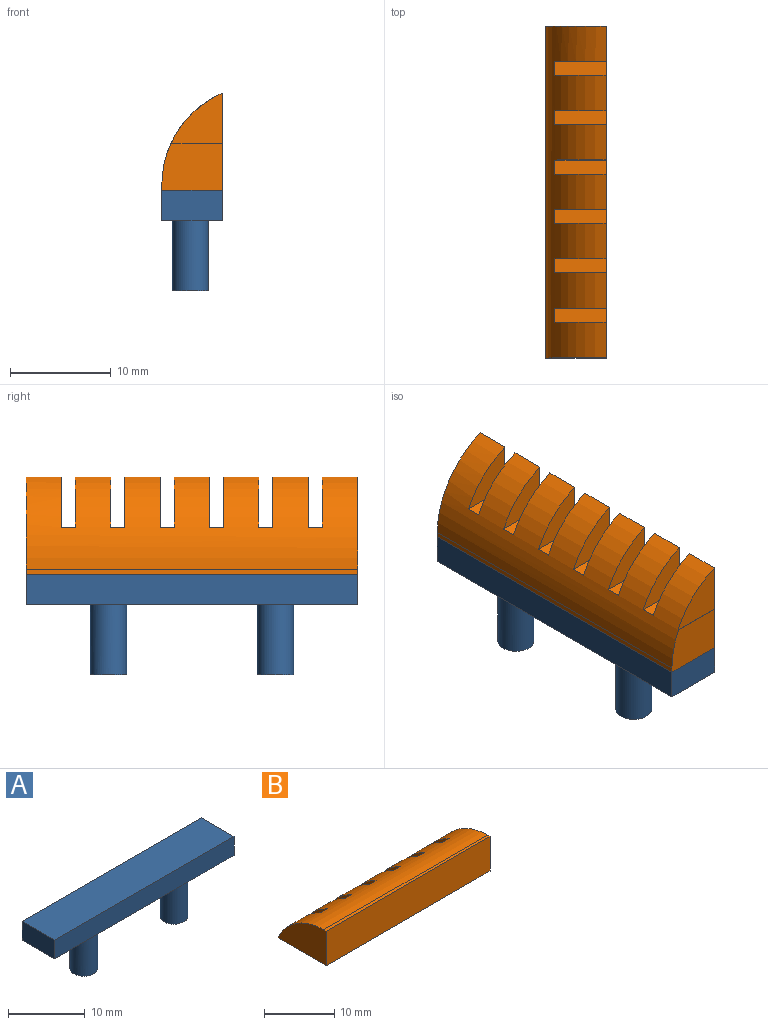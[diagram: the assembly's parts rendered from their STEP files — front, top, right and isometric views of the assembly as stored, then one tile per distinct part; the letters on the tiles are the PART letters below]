
ASSEMBLY  parts=2 mates=1
PART A: 10 faces, bbox 33x6x10 mm
  f0: plane 33x6.01mm, normal (0,0,1), area 198.3mm2, adj f2,f3,f4,f9
  f1: plane 33x6.01mm, normal (0,0,-1), area 178mm2, adj f2,f3,f4,f5,f7,f9
  f2: plane 6.01x3mm, normal (-1,0,0), area 18mm2, adj f0,f1,f4,f9
  f3: plane 6.01x3mm, normal (1,0,0), area 18mm2, adj f0,f1,f4,f9
  f4: plane 33x3mm, normal (0,1,0), area 99mm2, adj f0,f1,f2,f3
  f5: cylinder r=1.8mm len=7mm, axis (0,0,1), area 79.2mm2, adj f1,f6
  f6: plane 3.6x3.6mm, normal (0,0,-1), area 10.2mm2, adj f5
  f7: cylinder r=1.8mm len=7mm, axis (0,0,1), area 79.2mm2, adj f1,f8
  f8: plane 3.6x3.6mm, normal (0,0,-1), area 10.2mm2, adj f7
  f9: plane 33x3mm, normal (0,-1,0), area 99mm2, adj f0,f1,f2,f3
PART B: 26 faces, bbox 33x9.7x6 mm
  f0: plane 5.1x1.41mm, normal (0,1,0), area 7.2mm2, adj f7,f13,f15,f24
  f1: plane 5.1x1.41mm, normal (0,1,0), area 7.2mm2, adj f7,f12,f13,f22
  f2: plane 5.1x1.41mm, normal (0,1,0), area 7.2mm2, adj f7,f13,f20,f23
  f3: plane 5.1x1.41mm, normal (0,1,0), area 7.2mm2, adj f7,f13,f18,f25
  f4: plane 5.1x1.41mm, normal (0,1,0), area 7.2mm2, adj f7,f13,f16,f19
  f5: plane 5.1x1.41mm, normal (0,1,0), area 7.2mm2, adj f7,f13,f14,f21
  f6: plane 33x0.51mm, normal (0,0,1), area 16.8mm2, adj f9,f10,f11,f13
  f7: plane 33x9.68mm, normal (0,0,-1), area 276.9mm2, adj f0,f1,f2,f3,f4,f5,f8,f9
  f8: plane 5.1x0.04mm, normal (0,1,0), area 0.2mm2, adj f7,f10,f13,f17
  f9: plane 9.68x6.01mm, normal (-1,0,0), area 42.8mm2, adj f6,f7,f11,f13
  f10: plane 6.01x4.68mm, normal (1,0,0), area 26.9mm2, adj f6,f7,f8,f11,f13
  f11: plane 33x6.01mm, normal (0,-1,0), area 198.3mm2, adj f6,f7,f9,f10
  f12: plane 5.1x5mm, normal (1,0,0), area 15.9mm2, adj f1,f7,f13
  f13: cylinder r=10mm len=33mm, axis (1,0,0), area 320.8mm2, adj f0,f1,f2,f3,f4,f5,f6,f7
  f14: plane 5.1x5mm, normal (-1,0,0), area 15.9mm2, adj f5,f7,f13
  f15: plane 5.1x5mm, normal (1,0,0), area 15.9mm2, adj f0,f7,f13
  f16: plane 5.1x5mm, normal (-1,0,0), area 15.9mm2, adj f4,f7,f13
  f17: plane 5.1x5mm, normal (1,0,0), area 15.9mm2, adj f7,f8,f13
  f18: plane 5.1x5mm, normal (-1,0,0), area 15.9mm2, adj f3,f7,f13
  f19: plane 5.1x5mm, normal (1,0,0), area 15.9mm2, adj f4,f7,f13
  f20: plane 5.1x5mm, normal (-1,0,0), area 15.9mm2, adj f2,f7,f13
  f21: plane 5.1x5mm, normal (1,0,0), area 15.9mm2, adj f5,f7,f13
  f22: plane 5.1x5mm, normal (-1,0,0), area 15.9mm2, adj f1,f7,f13
  f23: plane 5.1x5mm, normal (1,0,0), area 15.9mm2, adj f2,f7,f13
  f24: plane 5.1x5mm, normal (-1,0,0), area 15.9mm2, adj f0,f7,f13
  f25: plane 5.1x5mm, normal (1,0,0), area 15.9mm2, adj f3,f7,f13
PLACE A rot(axis=(0,0,-1),90deg) t=(-13.41,13.74,33.97)mm
PLACE B rot(axis=(0.58,-0.58,-0.58),120deg) t=(-7.08,13.74,36.65)mm
MATE fastened B.f11 <-> A.f0  axis (0,0,-1) through (-10.08,-2.76,36.97)mm
